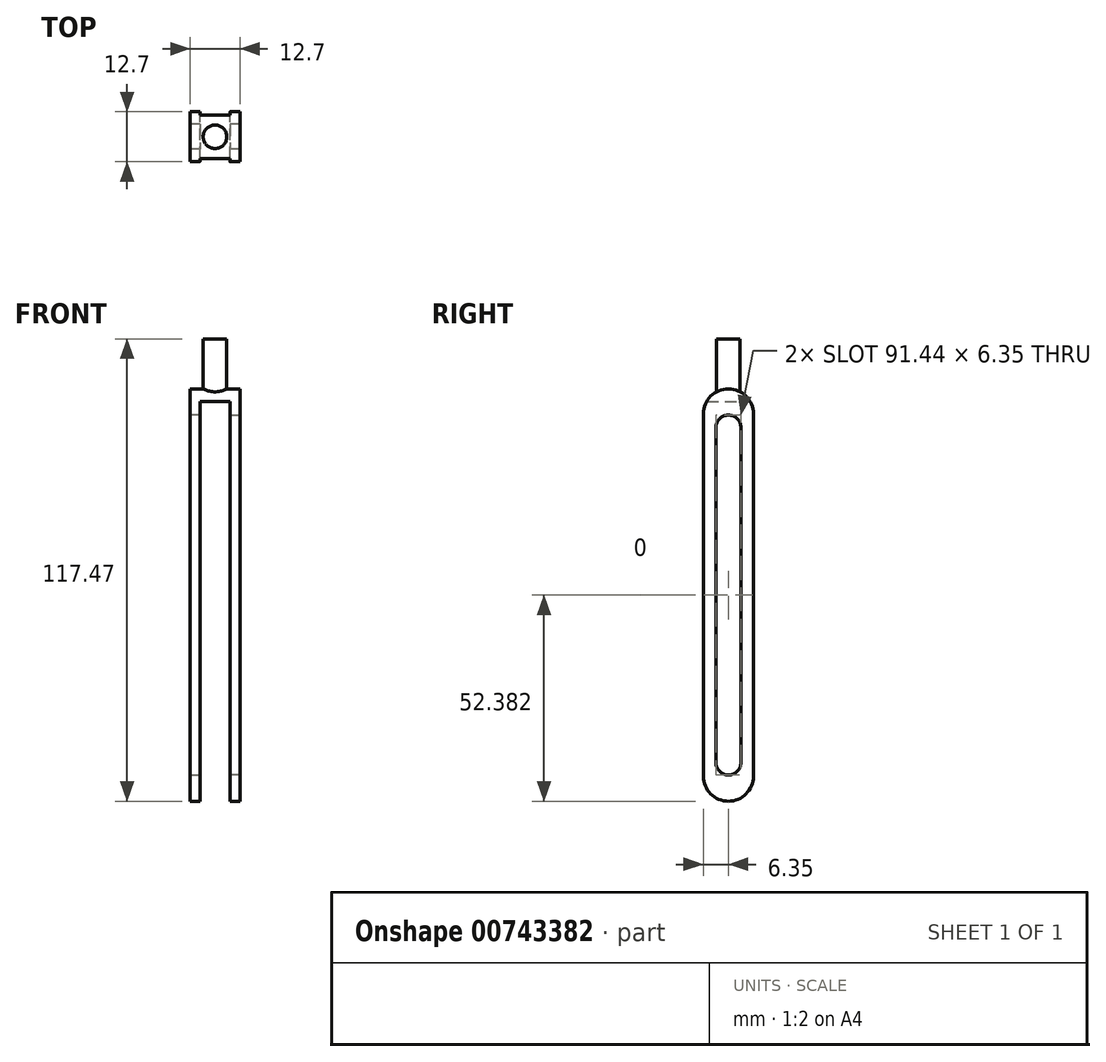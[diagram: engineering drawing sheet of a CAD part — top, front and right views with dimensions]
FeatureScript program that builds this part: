
annotation { "Feature Type Name" : "Feature", "Feature Type Description" : "" }
export const myFeature = defineFeature(function(context is Context, id is Id, definition is map)
    precondition{}
    {
        {
            var Q0;
            Q0=qCreatedBy(makeId("Top.planeOp"),FACE);
            var sketch = newSketch(context, id + "F0", { "sketchPlane" : qUnion([Q0])});
            skCircle(sketch, "E0", {"center": v(0, 0) * mm, "radius": 3 * mm});
            skSolve(sketch);
        }
        {
            var Q0;
            Q0 = qSketchRegion(id + "F0", true);
            extrude(context, id + "F1", {"entities" : qUnion([Q0]), "depth" : 12.7 * mm, "offsetDistance" : 25.4 * mm});
        }
        {
            var Q0;
            Q0=makeQuery(id+"F1.opExtrude","CAP_FACE",FACE,{"disambiguationData":[OSD([sQuery(id+"F0.wireOp",EDGE,"E0")])],"isStart":true});
            var sketch = newSketch(context, id + "F2", { "sketchPlane" : qUnion([Q0])});
            skLineSegment(sketch, "E1.bottom", {"start": v(6.35, -6.35) * mm, "end": v(-6.35, -6.35) * mm});
            skLineSegment(sketch, "E1.top", {"start": v(6.35, 6.35) * mm, "end": v(-6.35, 6.35) * mm});
            skLineSegment(sketch, "E1.left", {"start": v(6.35, -6.35) * mm, "end": v(6.35, 6.35) * mm});
            skLineSegment(sketch, "E1.right", {"start": v(-6.35, -6.35) * mm, "end": v(-6.35, 6.35) * mm});
            skPoint(sketch, "E1.middle", {"position": v(0, 0) * mm});
            skSolve(sketch);
        }
        {
            var Q0;
            Q0 = qSketchRegion(id + "F2", true);
            extrude(context, id + "F3", {"entities" : qUnion([Q0]), "operationType" : NewBodyOperationType.ADD, "depth" : 3.17 * mm, "offsetDistance" : 25.4 * mm});
        }
        {
            var Q0;
            Q0=makeQuery(id+"F3.opExtrude","CAP_FACE",FACE,{"disambiguationData":[OSD([sQuery(id+"F2.wireOp",EDGE,"E1.bottom"),sQuery(id+"F2.wireOp",EDGE,"E1.top"),sQuery(id+"F2.wireOp",EDGE,"E1.left"),sQuery(id+"F2.wireOp",EDGE,"E1.right")])],"isStart":false});
            var sketch = newSketch(context, id + "F4", { "sketchPlane" : qUnion([Q0])});
            skLineSegment(sketch, "E2.bottom", {"start": v(-6.35, 6.35) * mm, "end": v(-3.81, 6.35) * mm});
            skLineSegment(sketch, "E2.top", {"start": v(-6.35, -6.35) * mm, "end": v(-3.81, -6.35) * mm});
            skLineSegment(sketch, "E2.left", {"start": v(-6.35, 6.35) * mm, "end": v(-6.35, -6.35) * mm});
            skLineSegment(sketch, "E2.right", {"start": v(-3.81, 6.35) * mm, "end": v(-3.81, -6.35) * mm});
            skLineSegment(sketch, "E3.bottom", {"start": v(6.35, 6.35) * mm, "end": v(3.8, 6.35) * mm});
            skLineSegment(sketch, "E3.top", {"start": v(6.35, -6.35) * mm, "end": v(3.81, -6.35) * mm});
            skLineSegment(sketch, "E3.left", {"start": v(6.35, 6.35) * mm, "end": v(6.35, -6.35) * mm});
            skLineSegment(sketch, "E3.right", {"start": v(3.8, 6.35) * mm, "end": v(3.81, -6.35) * mm});
            skSolve(sketch);
        }
        {
            var Q0;
            Q0 = qSketchRegion(id + "F4", true);
            extrude(context, id + "F5", {"entities" : qUnion([Q0]), "operationType" : NewBodyOperationType.ADD, "depth" : 101.6 * mm, "offsetDistance" : 25.4 * mm});
        }
        {
            var Q0;
            Q0=makeQuery(id+"F5.opExtrude","CAP_EDGE",EDGE,{"disambiguationData":[OSD([sQuery(id+"F4.wireOp",EDGE,"E2.bottom")])],"isStart":false});
            var Q1;
            Q1=makeQuery(id+"F5.opExtrude","CAP_EDGE",EDGE,{"disambiguationData":[OSD([sQuery(id+"F4.wireOp",EDGE,"E2.top")])],"isStart":false});
            var Q2;
            Q2=makeQuery(id+"F5.opExtrude","CAP_EDGE",EDGE,{"disambiguationData":[OSD([sQuery(id+"F4.wireOp",EDGE,"E3.top")])],"isStart":false});
            var Q3;
            Q3=makeQuery(id+"F5.opExtrude","CAP_EDGE",EDGE,{"disambiguationData":[OSD([sQuery(id+"F4.wireOp",EDGE,"E3.bottom")])],"isStart":false});
            var Q4;
            Q4=makeQuery(id+"F3.opExtrude","CAP_EDGE",EDGE,{"disambiguationData":[OSD([sQuery(id+"F2.wireOp",EDGE,"E1.bottom")])],"isStart":true});
            var Q5;
            Q5=makeQuery(id+"F3.opExtrude","CAP_EDGE",EDGE,{"disambiguationData":[OSD([sQuery(id+"F2.wireOp",EDGE,"E1.top")])],"isStart":true});
            fillet(context, id + "F6", {"entities" : qUnion([Q0, Q1, Q2, Q3, Q4, Q5]), "radius" : 6.35 * mm, "tangentPropagation" : true, "allowEdgeOverflow" : false});
        }
        {
            var Q0;
            Q0=makeQuery(id+"F5.boolean.opBoolean","MERGE",FACE,{"derivedFrom":[makeQuery(id+"F3.opExtrude","SWEPT_FACE",FACE,{"disambiguationData":[OSD([sQuery(id+"F2.wireOp",EDGE,"E1.right")])]}),makeQuery(id+"F5.opExtrude","SWEPT_FACE",FACE,{"disambiguationData":[OSD([sQuery(id+"F4.wireOp",EDGE,"E2.left")])]})]});
            var sketch = newSketch(context, id + "F7", { "sketchPlane" : qUnion([Q0])});
            skLineSegment(sketch, "E4", {"start": v(0, 0) * mm, "end": v(0, -104.78) * mm});
            skLineSegment(sketch, "E5.bottom", {"start": v(-3.18, -98.1) * mm, "end": v(3.17, -98.1) * mm});
            skLineSegment(sketch, "E5.top", {"start": v(-3.18, -6.67) * mm, "end": v(3.17, -6.67) * mm});
            skLineSegment(sketch, "E5.left", {"start": v(-3.18, -98.1) * mm, "end": v(-3.18, -6.67) * mm});
            skLineSegment(sketch, "E5.right", {"start": v(3.17, -98.1) * mm, "end": v(3.17, -6.67) * mm});
            skPoint(sketch, "E5.middle", {"position": v(0, -52.39) * mm});
            skSolve(sketch);
        }
        {
            var Q0;
            Q0 = qSketchRegion(id + "F7", true);
            extrude(context, id + "F8", {"entities" : qUnion([Q0]), "operationType" : NewBodyOperationType.REMOVE, "oppositeDirection" : true, "depth" : 25.4 * mm, "offsetDistance" : 25.4 * mm});
        }
        {
            var Q0;
            {var subQ0=sQuery(id+"F7.wireOp",EDGE,"E5.bottom");var subQ1=sQuery(id+"F7.wireOp",EDGE,"E5.right");Q0=makeQuery(id+"F8.boolean.opBoolean","COPY",EDGE,{"disambiguationData":[TD([makeQuery(id+"F3.opExtrude","SWEPT_FACE",FACE,{"disambiguationData":[OSD([sQuery(id+"F2.wireOp",EDGE,"E1.right")])]})])],"derivedFrom":makeQuery(id+"F8.opExtrude","SWEPT_EDGE",EDGE,{"disambiguationData":[OSD([subQ0,subQ1])]})});}
            var Q1;
            {var subQ0=sQuery(id+"F7.wireOp",EDGE,"E5.top");var subQ1=sQuery(id+"F7.wireOp",EDGE,"E5.right");Q1=makeQuery(id+"F8.boolean.opBoolean","COPY",EDGE,{"disambiguationData":[TD([makeQuery(id+"F3.opExtrude","SWEPT_FACE",FACE,{"disambiguationData":[OSD([sQuery(id+"F2.wireOp",EDGE,"E1.right")])]})])],"derivedFrom":makeQuery(id+"F8.opExtrude","SWEPT_EDGE",EDGE,{"disambiguationData":[OSD([subQ0,subQ1])]})});}
            var Q2;
            {var subQ0=sQuery(id+"F7.wireOp",EDGE,"E5.top");var subQ1=sQuery(id+"F7.wireOp",EDGE,"E5.left");Q2=makeQuery(id+"F8.boolean.opBoolean","COPY",EDGE,{"disambiguationData":[TD([makeQuery(id+"F3.opExtrude","SWEPT_FACE",FACE,{"disambiguationData":[OSD([sQuery(id+"F2.wireOp",EDGE,"E1.right")])]})])],"derivedFrom":makeQuery(id+"F8.opExtrude","SWEPT_EDGE",EDGE,{"disambiguationData":[OSD([subQ0,subQ1])]})});}
            var Q3;
            {var subQ0=sQuery(id+"F7.wireOp",EDGE,"E5.top");var subQ1=sQuery(id+"F7.wireOp",EDGE,"E5.left");Q3=makeQuery(id+"F8.boolean.opBoolean","COPY",EDGE,{"disambiguationData":[TD([makeQuery(id+"F3.opExtrude","SWEPT_FACE",FACE,{"disambiguationData":[OSD([sQuery(id+"F2.wireOp",EDGE,"E1.left")])]})])],"derivedFrom":makeQuery(id+"F8.opExtrude","SWEPT_EDGE",EDGE,{"disambiguationData":[OSD([subQ0,subQ1])]})});}
            var Q4;
            {var subQ0=sQuery(id+"F7.wireOp",EDGE,"E5.top");var subQ1=sQuery(id+"F7.wireOp",EDGE,"E5.right");Q4=makeQuery(id+"F8.boolean.opBoolean","COPY",EDGE,{"disambiguationData":[TD([makeQuery(id+"F3.opExtrude","SWEPT_FACE",FACE,{"disambiguationData":[OSD([sQuery(id+"F2.wireOp",EDGE,"E1.left")])]})])],"derivedFrom":makeQuery(id+"F8.opExtrude","SWEPT_EDGE",EDGE,{"disambiguationData":[OSD([subQ0,subQ1])]})});}
            var Q5;
            {var subQ0=sQuery(id+"F7.wireOp",EDGE,"E5.bottom");var subQ1=sQuery(id+"F7.wireOp",EDGE,"E5.left");Q5=makeQuery(id+"F8.boolean.opBoolean","COPY",EDGE,{"disambiguationData":[TD([makeQuery(id+"F3.opExtrude","SWEPT_FACE",FACE,{"disambiguationData":[OSD([sQuery(id+"F2.wireOp",EDGE,"E1.right")])]})])],"derivedFrom":makeQuery(id+"F8.opExtrude","SWEPT_EDGE",EDGE,{"disambiguationData":[OSD([subQ0,subQ1])]})});}
            var Q6;
            {var subQ0=sQuery(id+"F7.wireOp",EDGE,"E5.bottom");var subQ1=sQuery(id+"F7.wireOp",EDGE,"E5.left");Q6=makeQuery(id+"F8.boolean.opBoolean","COPY",EDGE,{"disambiguationData":[TD([makeQuery(id+"F3.opExtrude","SWEPT_FACE",FACE,{"disambiguationData":[OSD([sQuery(id+"F2.wireOp",EDGE,"E1.left")])]})])],"derivedFrom":makeQuery(id+"F8.opExtrude","SWEPT_EDGE",EDGE,{"disambiguationData":[OSD([subQ0,subQ1])]})});}
            var Q7;
            {var subQ0=sQuery(id+"F7.wireOp",EDGE,"E5.bottom");var subQ1=sQuery(id+"F7.wireOp",EDGE,"E5.right");Q7=makeQuery(id+"F8.boolean.opBoolean","COPY",EDGE,{"disambiguationData":[TD([makeQuery(id+"F3.opExtrude","SWEPT_FACE",FACE,{"disambiguationData":[OSD([sQuery(id+"F2.wireOp",EDGE,"E1.left")])]})])],"derivedFrom":makeQuery(id+"F8.opExtrude","SWEPT_EDGE",EDGE,{"disambiguationData":[OSD([subQ0,subQ1])]})});}
            fillet(context, id + "F9", {"entities" : qUnion([Q0, Q1, Q2, Q3, Q4, Q5, Q6, Q7]), "radius" : 3.17 * mm, "tangentPropagation" : true, "allowEdgeOverflow" : false});
        }
    });
